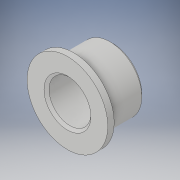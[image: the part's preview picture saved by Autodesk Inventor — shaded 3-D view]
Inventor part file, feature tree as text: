
AUTODESK INVENTOR PART (.ipt)
format: ipt  version: 2017 (Build 210142000, 142)  size: 124,928 bytes
history: native  units: in
note: dims shown in document units (in); Inventor stores cm internally (conversion verified against a paired STEP export)
features: sketch x3, extrude x2, chamfer x1
ambient origin geometry x8: Origin, YZ Plane, XZ Plane, XY Plane, X Axis, Y Axis, Z Axis, Center Point
bodies: Solid1 (feature_tree)
feature tree (6):
  sketch  "Sketch1"  dims[d0=0.329in d1=0.5in]
  extrude  "Extrusion1"  Depth=0.5in
  extrude  "Extrusion2"  Depth=0.05in
  chamfer  "Chamfer1"  Distance=0.05in
  sketch  "Sketch2"  dims[d2=0.305in d3=0.0in d4=0.635in d5=0.05in d6=0.0in]
  sketch  "Sketch3"  dims[d7=0.02in d8=0.125in d9=45.0deg]
